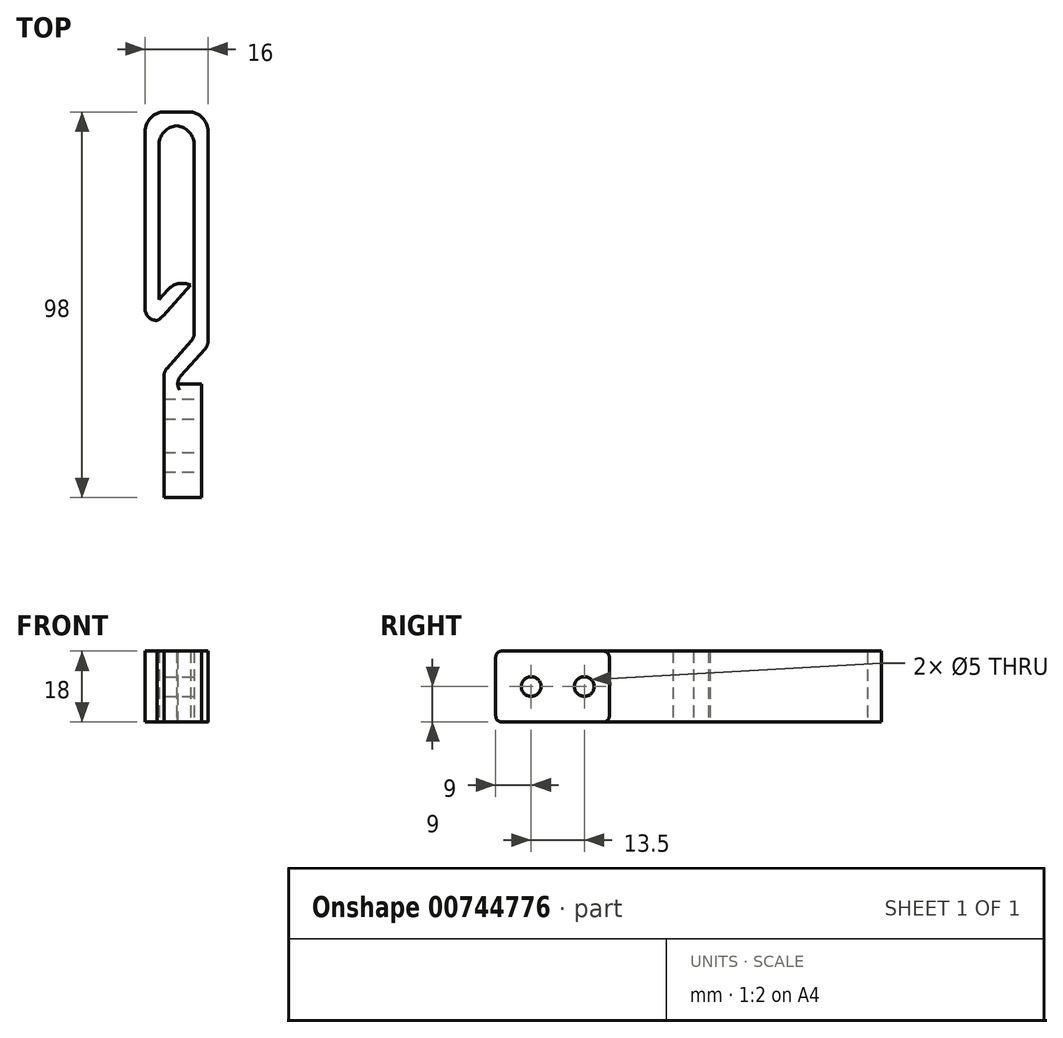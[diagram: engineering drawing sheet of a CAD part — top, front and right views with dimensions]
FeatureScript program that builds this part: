
annotation { "Feature Type Name" : "Feature", "Feature Type Description" : "" }
export const myFeature = defineFeature(function(context is Context, id is Id, definition is map)
    precondition{}
    {
        {
            var Q0;
            Q0=qCreatedBy(makeId("Top.planeOp"),FACE);
            var sketch = newSketch(context, id + "F0", { "sketchPlane" : qUnion([Q0])});
            skLineSegment(sketch, "E0.bottom", {"start": v(8, -49) * mm, "end": v(-8, -49) * mm});
            skLineSegment(sketch, "E0.top", {"start": v(8, 49) * mm, "end": v(-8, 49) * mm});
            skLineSegment(sketch, "E0.left", {"start": v(8, -49) * mm, "end": v(8, 49) * mm});
            skLineSegment(sketch, "E0.right", {"start": v(-8, -49) * mm, "end": v(-8, 49) * mm});
            skPoint(sketch, "E0.middle", {"position": v(0, 0) * mm});
            skLineSegment(sketch, "E1", {"start": v(4.5, 49) * mm, "end": v(4.5, -19) * mm});
            skLineSegment(sketch, "E2", {"start": v(-8, 45.5) * mm, "end": v(8, 45.5) * mm});
            skLineSegment(sketch, "E3", {"start": v(3.5, 49) * mm, "end": v(3.5, -19) * mm, "construction": true});
            skLineSegment(sketch, "E4.bottom", {"start": v(-8, 49) * mm, "end": v(-4.5, 49) * mm});
            skLineSegment(sketch, "E4.top", {"start": v(-8, -4) * mm, "end": v(-4.5, -4) * mm});
            skLineSegment(sketch, "E4.left", {"start": v(-8, 49) * mm, "end": v(-8, -4) * mm});
            skLineSegment(sketch, "E4.right", {"start": v(-4.5, 49) * mm, "end": v(-4.5, -4) * mm});
            skLineSegment(sketch, "E5", {"start": v(-4.5, -4) * mm, "end": v(3.5, 5) * mm});
            skLineSegment(sketch, "E6", {"start": v(3.5, 5) * mm, "end": v(0.88, 7.33) * mm});
            skLineSegment(sketch, "E7", {"start": v(0.88, 7.33) * mm, "end": v(-8, -2.67) * mm});
            skLineSegment(sketch, "E8", {"start": v(-8, -19) * mm, "end": v(8, -19) * mm, "construction": true});
            skLineSegment(sketch, "E9.bottom", {"start": v(-3.2, -49) * mm, "end": v(0.3, -49) * mm});
            skLineSegment(sketch, "E9.top", {"start": v(-3.2, -19) * mm, "end": v(0.3, -19) * mm});
            skLineSegment(sketch, "E9.left", {"start": v(-3.2, -49) * mm, "end": v(-3.2, -19) * mm});
            skLineSegment(sketch, "E9.right", {"start": v(0.3, -49) * mm, "end": v(0.3, -19) * mm});
            skLineSegment(sketch, "E10", {"start": v(0.3, -19) * mm, "end": v(8, -10.34) * mm});
            skLineSegment(sketch, "E11", {"start": v(-3.2, -19) * mm, "end": v(-3.2, -17) * mm});
            skLineSegment(sketch, "E12", {"start": v(-3.2, -17) * mm, "end": v(4.5, -8.34) * mm});
            skSolve(sketch);
        }
        {
            var Q0;
            {var subQ0=sQuery(id+"F0.wireOp",EDGE,"E0.right");var subQ1=sQuery(id+"F0.wireOp",EDGE,"E0.top");var subQ2=makeQuery(id+"F0.imprint","INTERSECT",VERTEX,{"derivedFrom":[subQ1,subQ0]});Q0=makeQuery(id+"F0.imprint","IMPRINT",FACE,{"disambiguationData":[TD([[makeQuery(id+"F0.imprint","IMPRINT",EDGE,{"disambiguationData":[TD([[subQ2,1.0]])],"derivedFrom":subQ1}),1.0]])]});}
            var Q1;
            {var subQ0=sQuery(id+"F0.wireOp",EDGE,"E1");var subQ1=sQuery(id+"F0.wireOp",EDGE,"E0.top");var subQ2=makeQuery(id+"F0.imprint","INTERSECT",VERTEX,{"derivedFrom":[subQ1,subQ0]});Q1=makeQuery(id+"F0.imprint","IMPRINT",FACE,{"disambiguationData":[TD([[makeQuery(id+"F0.imprint","IMPRINT",EDGE,{"disambiguationData":[TD([[subQ2,-1.0]])],"derivedFrom":subQ1}),1.0]])]});}
            var Q2;
            {var subQ0=sQuery(id+"F0.wireOp",EDGE,"E1");var subQ1=sQuery(id+"F0.wireOp",EDGE,"E0.top");var subQ2=makeQuery(id+"F0.imprint","INTERSECT",VERTEX,{"derivedFrom":[subQ1,subQ0]});Q2=makeQuery(id+"F0.imprint","IMPRINT",FACE,{"disambiguationData":[TD([[makeQuery(id+"F0.imprint","IMPRINT",EDGE,{"disambiguationData":[TD([[subQ2,1.0]])],"derivedFrom":subQ1}),1.0]])]});}
            var Q3;
            {var subQ3=sQuery(id+"F0.wireOp",EDGE,"E0.left");var subQ5=sQuery(id+"F0.wireOp",EDGE,"E10");var subQ6=makeQuery(id+"F0.imprint","INTERSECT",VERTEX,{"derivedFrom":[subQ3,subQ5]});Q3=makeQuery(id+"F0.imprint","IMPRINT",FACE,{"disambiguationData":[TD([[makeQuery(id+"F0.imprint","IMPRINT",EDGE,{"disambiguationData":[TD([[subQ6,-1.0]])],"derivedFrom":subQ3}),1.0]])]});}
            var Q4;
            {var subQ0=sQuery(id+"F0.wireOp",EDGE,"E7");var subQ1=sQuery(id+"F0.wireOp",EDGE,"E0.right");var subQ2=makeQuery(id+"F0.imprint","INTERSECT",VERTEX,{"derivedFrom":[subQ1,subQ0]});Q4=makeQuery(id+"F0.imprint","IMPRINT",FACE,{"disambiguationData":[TD([[makeQuery(id+"F0.imprint","IMPRINT",EDGE,{"disambiguationData":[TD([[subQ2,-1.0]])],"derivedFrom":subQ1}),-1.0]])]});}
            var Q5;
            {var subQ3=sQuery(id+"F0.wireOp",EDGE,"E4.top");Q5=makeQuery(id+"F0.imprint","IMPRINT",FACE,{"disambiguationData":[TD([[makeQuery(id+"F0.imprint","IMPRINT",EDGE,{"derivedFrom":subQ3}),1.0]])]});}
            var Q6;
            {var subQ0=sQuery(id+"F0.wireOp",EDGE,"E5");Q6=makeQuery(id+"F0.imprint","IMPRINT",FACE,{"disambiguationData":[TD([[makeQuery(id+"F0.imprint","IMPRINT",EDGE,{"derivedFrom":subQ0}),1.0]])]});}
            var Q7;
            {var subQ1=sQuery(id+"F0.wireOp",EDGE,"E9.top");Q7=makeQuery(id+"F0.imprint","IMPRINT",FACE,{"disambiguationData":[TD([[makeQuery(id+"F0.imprint","IMPRINT",EDGE,{"derivedFrom":subQ1}),1.0]])]});}
            var Q8;
            Q8=makeQuery(id+"F0.imprint","IMPRINT",FACE,{"disambiguationData":[TD([[makeQuery(id+"F0.imprint","IMPRINT",EDGE,{"derivedFrom":sQuery(id+"F0.wireOp",EDGE,"E9.top")}),-1.0]])]});
            extrude(context, id + "F1", {"entities" : qUnion([Q0, Q1, Q2, Q3, Q4, Q5, Q6, Q7, Q8]), "depth" : 18 * mm, "offsetDistance" : 25 * mm});
        }
        {
            var Q0;
            Q0=makeQuery(id+"F1.opExtrude","SWEPT_EDGE",EDGE,{"disambiguationData":[OSD([sQuery(id+"F0.wireOp",EDGE,"E0.left"),sQuery(id+"F0.wireOp",EDGE,"E10")])]});
            var Q1;
            Q1=makeQuery(id+"F1.opExtrude","SWEPT_EDGE",EDGE,{"disambiguationData":[OSD([sQuery(id+"F0.wireOp",EDGE,"E11"),sQuery(id+"F0.wireOp",EDGE,"E12")])]});
            var Q2;
            Q2=makeQuery(id+"F1.opExtrude","SWEPT_EDGE",EDGE,{"disambiguationData":[OSD([sQuery(id+"F0.wireOp",EDGE,"E1"),sQuery(id+"F0.wireOp",EDGE,"E12")])]});
            var Q3;
            Q3=makeQuery(id+"F1.opExtrude","SWEPT_EDGE",EDGE,{"disambiguationData":[OSD([sQuery(id+"F0.wireOp",EDGE,"E0.right"),sQuery(id+"F0.wireOp",EDGE,"E4.top")])]});
            var Q4;
            Q4=makeQuery(id+"F1.opExtrude","SWEPT_EDGE",EDGE,{"disambiguationData":[OSD([sQuery(id+"F0.wireOp",EDGE,"E9.top"),sQuery(id+"F0.wireOp",EDGE,"E9.right"),sQuery(id+"F0.wireOp",EDGE,"E10")])]});
            fillet(context, id + "F2", {"entities" : qUnion([Q0, Q1, Q2, Q3, Q4]), "radius" : 3 * mm, "tangentPropagation" : true, "allowEdgeOverflow" : false});
        }
        {
            var Q0;
            Q0=makeQuery(id+"F1.opExtrude","SWEPT_EDGE",EDGE,{"disambiguationData":[OSD([sQuery(id+"F0.wireOp",EDGE,"E2"),sQuery(id+"F0.wireOp",EDGE,"E4.right")])]});
            var Q1;
            Q1=makeQuery(id+"F1.opExtrude","SWEPT_EDGE",EDGE,{"disambiguationData":[OSD([sQuery(id+"F0.wireOp",EDGE,"E1"),sQuery(id+"F0.wireOp",EDGE,"E2")])]});
            var Q2;
            Q2=makeQuery(id+"F1.opExtrude","SWEPT_EDGE",EDGE,{"disambiguationData":[OSD([sQuery(id+"F0.wireOp",EDGE,"E0.top"),sQuery(id+"F0.wireOp",EDGE,"E0.left")])]});
            var Q3;
            Q3=makeQuery(id+"F1.opExtrude","SWEPT_EDGE",EDGE,{"disambiguationData":[OSD([sQuery(id+"F0.wireOp",EDGE,"E0.top"),sQuery(id+"F0.wireOp",EDGE,"E0.right")])]});
            var Q4;
            Q4=makeQuery(id+"F1.opExtrude","SWEPT_EDGE",EDGE,{"disambiguationData":[OSD([sQuery(id+"F0.wireOp",EDGE,"E4.top"),sQuery(id+"F0.wireOp",EDGE,"E4.right"),sQuery(id+"F0.wireOp",EDGE,"E5")])]});
            var Q5;
            Q5=makeQuery(id+"F1.opExtrude","SWEPT_EDGE",EDGE,{"disambiguationData":[OSD([sQuery(id+"F0.wireOp",EDGE,"E6"),sQuery(id+"F0.wireOp",EDGE,"E7")])]});
            fillet(context, id + "F3", {"entities" : qUnion([Q0, Q1, Q2, Q3, Q4, Q5]), "radius" : 5 * mm, "tangentPropagation" : true, "allowEdgeOverflow" : false});
        }
        {
            var Q0;
            Q0=makeQuery(id+"F1.opExtrude","SWEPT_FACE",FACE,{"disambiguationData":[OSD([sQuery(id+"F0.wireOp",EDGE,"E9.right")])]});
            var sketch = newSketch(context, id + "F4", { "sketchPlane" : qUnion([Q0])});
            skLineSegment(sketch, "E13", {"start": v(-49, 9) * mm, "end": v(-20.14, 9) * mm, "construction": true});
            skCircle(sketch, "E14", {"center": v(-40, 9) * mm, "radius": 2.5 * mm});
            skCircle(sketch, "E15", {"center": v(-26.5, 9) * mm, "radius": 2.5 * mm});
            skSolve(sketch);
        }
        {
            var Q0;
            Q0=makeQuery(id+"F4.imprint","IMPRINT",FACE,{"disambiguationData":[TD([[makeQuery(id+"F4.imprint","IMPRINT",EDGE,{"derivedFrom":sQuery(id+"F4.wireOp",EDGE,"E14")}),1.0]])]});
            var Q1;
            Q1=makeQuery(id+"F4.imprint","IMPRINT",FACE,{"disambiguationData":[TD([[makeQuery(id+"F4.imprint","IMPRINT",EDGE,{"derivedFrom":sQuery(id+"F4.wireOp",EDGE,"E15")}),1.0]])]});
            extrude(context, id + "F5", {"entities" : qUnion([Q0, Q1]), "operationType" : NewBodyOperationType.REMOVE, "endBound" : BoundingType.UP_TO_NEXT, "oppositeDirection" : true, "depth" : 25 * mm, "offsetDistance" : 25 * mm});
        }
        {
            var Q0;
            Q0=makeQuery(id+"F4.imprint","IMPRINT",FACE,{"disambiguationData":[TD([[makeQuery(id+"F4.imprint","IMPRINT",EDGE,{"derivedFrom":sQuery(id+"F4.wireOp",EDGE,"E14")}),-1.0]])]});
            extrude(context, id + "F6", {"entities" : qUnion([Q0]), "operationType" : NewBodyOperationType.ADD, "depth" : 6 * mm, "offsetDistance" : 25 * mm});
        }
        {
            var Q0;
            {var subQ0=sQuery(id+"F0.wireOp",EDGE,"E9.right");var subQ1=sQuery(id+"F0.wireOp",EDGE,"E0.bottom");Q0=makeQuery(id+"F6.boolean.opBoolean","MERGE",EDGE,{"derivedFrom":[makeQuery(id+"F1.opExtrude","CAP_EDGE",EDGE,{"disambiguationData":[OSD([subQ1])],"isStart":false}),makeQuery(id+"F6.opExtrude","SWEPT_EDGE",EDGE,{"disambiguationData":[OSD([subQ1,subQ0]),TDD([makeQuery(id+"F4.imprint","INTERSECT",VERTEX,{"derivedFrom":[makeQuery(id+"F1.opExtrude","SWEPT_EDGE",EDGE,{"disambiguationData":[OSD([subQ1,subQ0])]}),makeQuery(id+"F1.opExtrude","CAP_EDGE",EDGE,{"disambiguationData":[OSD([subQ0])],"isStart":false})]})])]})]});}
            var Q1;
            {var subQ0=sQuery(id+"F0.wireOp",EDGE,"E9.right");var subQ1=sQuery(id+"F0.wireOp",EDGE,"E0.bottom");Q1=makeQuery(id+"F6.boolean.opBoolean","MERGE",EDGE,{"derivedFrom":[makeQuery(id+"F1.opExtrude","CAP_EDGE",EDGE,{"disambiguationData":[OSD([subQ1])],"isStart":true}),makeQuery(id+"F6.opExtrude","SWEPT_EDGE",EDGE,{"disambiguationData":[OSD([subQ1,subQ0]),TDD([makeQuery(id+"F4.imprint","INTERSECT",VERTEX,{"derivedFrom":[makeQuery(id+"F1.opExtrude","SWEPT_EDGE",EDGE,{"disambiguationData":[OSD([subQ1,subQ0])]}),makeQuery(id+"F1.opExtrude","CAP_EDGE",EDGE,{"disambiguationData":[OSD([subQ0])],"isStart":true})]})])]})]});}
            var Q2;
            {var subQ0=sQuery(id+"F0.wireOp",EDGE,"E9.right");var subQ1=sQuery(id+"F0.wireOp",EDGE,"E10");var subQ2=sQuery(id+"F0.wireOp",EDGE,"E9.top");Q2=makeQuery(id+"F6.opExtrude","SWEPT_EDGE",EDGE,{"disambiguationData":[OSD([subQ2,subQ0,subQ1]),TDD([makeQuery(id+"F4.imprint","INTERSECT",VERTEX,{"derivedFrom":[makeQuery(id+"F2.opFillet","BLEND_EDGE",EDGE,{"blendedFrom":[makeQuery(id+"F1.opExtrude","SWEPT_EDGE",EDGE,{"disambiguationData":[OSD([subQ2,subQ0,subQ1])]}),makeQuery(id+"F1.opExtrude","SWEPT_FACE",FACE,{"disambiguationData":[OSD([subQ0])]})],"blendedInto":[makeQuery(id+"F1.opExtrude","SWEPT_FACE",FACE,{"disambiguationData":[OSD([subQ0])]})]}),makeQuery(id+"F1.opExtrude","CAP_EDGE",EDGE,{"disambiguationData":[OSD([subQ0])],"isStart":false})]})])]});}
            var Q3;
            {var subQ0=sQuery(id+"F0.wireOp",EDGE,"E9.right");var subQ1=sQuery(id+"F0.wireOp",EDGE,"E10");var subQ2=sQuery(id+"F0.wireOp",EDGE,"E9.top");Q3=makeQuery(id+"F6.opExtrude","SWEPT_EDGE",EDGE,{"disambiguationData":[OSD([subQ2,subQ0,subQ1]),TDD([makeQuery(id+"F4.imprint","INTERSECT",VERTEX,{"derivedFrom":[makeQuery(id+"F2.opFillet","BLEND_EDGE",EDGE,{"blendedFrom":[makeQuery(id+"F1.opExtrude","SWEPT_EDGE",EDGE,{"disambiguationData":[OSD([subQ2,subQ0,subQ1])]}),makeQuery(id+"F1.opExtrude","SWEPT_FACE",FACE,{"disambiguationData":[OSD([subQ0])]})],"blendedInto":[makeQuery(id+"F1.opExtrude","SWEPT_FACE",FACE,{"disambiguationData":[OSD([subQ0])]})]}),makeQuery(id+"F1.opExtrude","CAP_EDGE",EDGE,{"disambiguationData":[OSD([subQ0])],"isStart":true})]})])]});}
            fillet(context, id + "F7", {"entities" : qUnion([Q0, Q1, Q2, Q3]), "radius" : 1.5 * mm, "tangentPropagation" : true, "allowEdgeOverflow" : false});
        }
    });
